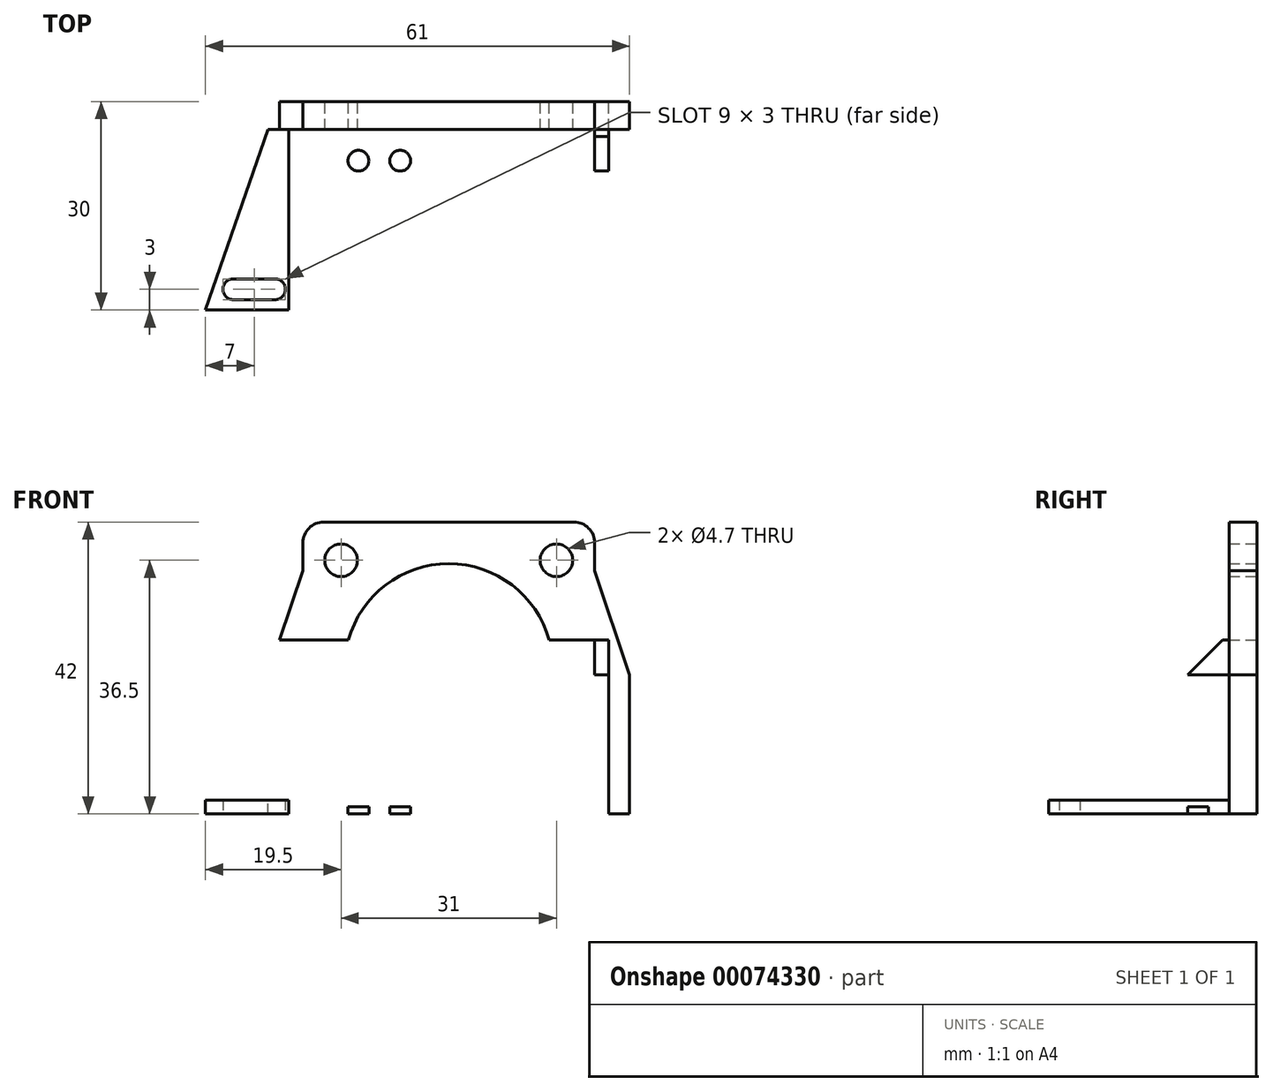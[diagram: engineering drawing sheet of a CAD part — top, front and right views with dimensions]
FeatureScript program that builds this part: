
annotation { "Feature Type Name" : "Feature", "Feature Type Description" : "" }
export const myFeature = defineFeature(function(context is Context, id is Id, definition is map)
    precondition{}
    {
        {
            var Q0;
            Q0=qCreatedBy(makeId("Front.planeOp"),FACE);
            var sketch = newSketch(context, id + "F0", { "sketchPlane" : qUnion([Q0])});
            skLineSegment(sketch, "E0.rect.bottom", {"start": v(21, 21) * mm, "end": v(-21, 21) * mm});
            skLineSegment(sketch, "E0.rect.top", {"start": v(21, -21) * mm, "end": v(-21, -21) * mm});
            skLineSegment(sketch, "E0.rect.left", {"start": v(21, 21) * mm, "end": v(21, -21) * mm});
            skLineSegment(sketch, "E0.rect.right", {"start": v(-21, 21) * mm, "end": v(-21, -21) * mm});
            skPoint(sketch, "E0.rect.middle", {"position": v(0, 0) * mm});
            skCircle(sketch, "E1", {"center": v(0, 0) * mm, "radius": 15 * mm});
            skCircle(sketch, "E2", {"center": v(-15.5, 15.5) * mm, "radius": 2.35 * mm});
            skCircle(sketch, "E3.MirrorC", {"center": v(15.5, 15.5) * mm, "radius": 2.35 * mm});
            skCircle(sketch, "E4.MirrorC", {"center": v(15.5, -15.5) * mm, "radius": 2.35 * mm});
            skCircle(sketch, "E5.MirrorC", {"center": v(-15.5, -15.5) * mm, "radius": 2.35 * mm});
            skLineSegment(sketch, "E6.bottom", {"start": v(21, -21) * mm, "end": v(26, -21) * mm});
            skLineSegment(sketch, "E6.top", {"start": v(21, -1) * mm, "end": v(26, -1) * mm});
            skLineSegment(sketch, "E6.left", {"start": v(21, -21) * mm, "end": v(21, -1) * mm});
            skLineSegment(sketch, "E6.right", {"start": v(26, -21) * mm, "end": v(26, -1) * mm});
            skLineSegment(sketch, "E7.MirrorCS", {"start": v(-21, -1) * mm, "end": v(-26, -1) * mm});
            skLineSegment(sketch, "E8.MirrorCS", {"start": v(-26, -21) * mm, "end": v(-26, -1) * mm});
            skLineSegment(sketch, "E9", {"start": v(26, -1) * mm, "end": v(21, 14) * mm});
            skLineSegment(sketch, "E10.MirrorCS", {"start": v(-26, -1) * mm, "end": v(-21, 14) * mm});
            skLineSegment(sketch, "E11.MirrorCS", {"start": v(-21, -21) * mm, "end": v(-26, -21) * mm});
            skLineSegment(sketch, "E12", {"start": v(-21, -20) * mm, "end": v(21, -20) * mm});
            skLineSegment(sketch, "E13.bottom", {"start": v(21, -21) * mm, "end": v(23, -21) * mm});
            skLineSegment(sketch, "E13.top", {"start": v(21, 4) * mm, "end": v(23, 4) * mm});
            skLineSegment(sketch, "E13.left", {"start": v(21, -21) * mm, "end": v(21, 4) * mm});
            skLineSegment(sketch, "E13.right", {"start": v(23, -21) * mm, "end": v(23, 4) * mm});
            skLineSegment(sketch, "E14.MirrorCS", {"start": v(-21, 4) * mm, "end": v(-23, 4) * mm});
            skLineSegment(sketch, "E15.MirrorCS", {"start": v(-23, -21) * mm, "end": v(-23, 4) * mm});
            skSolve(sketch);
        }
        {
            var Q0;
            {var subQ3=sQuery(id+"F0.wireOp",EDGE,"E0.rect.bottom");Q0=makeQuery(id+"F0.imprint","IMPRINT",FACE,{"disambiguationData":[TD([[makeQuery(id+"F0.imprint","IMPRINT",EDGE,{"derivedFrom":subQ3}),1.0]])]});}
            var Q1;
            {var subQ1=sQuery(id+"F0.wireOp",EDGE,"E9");Q1=makeQuery(id+"F0.imprint","IMPRINT",FACE,{"disambiguationData":[TD([[makeQuery(id+"F0.imprint","IMPRINT",EDGE,{"derivedFrom":subQ1}),1.0]])]});}
            var Q2;
            {var subQ1=sQuery(id+"F0.wireOp",EDGE,"E10.MirrorCS");Q2=makeQuery(id+"F0.imprint","IMPRINT",FACE,{"disambiguationData":[TD([[makeQuery(id+"F0.imprint","IMPRINT",EDGE,{"derivedFrom":subQ1}),-1.0]])]});}
            var Q3;
            {var subQ0=sQuery(id+"F0.wireOp",EDGE,"E6.bottom");Q3=makeQuery(id+"F0.imprint","IMPRINT",FACE,{"disambiguationData":[TD([[makeQuery(id+"F0.imprint","IMPRINT",EDGE,{"derivedFrom":subQ0}),1.0]])]});}
            var Q4;
            {var subQ0=sQuery(id+"F0.wireOp",EDGE,"E8.MirrorCS");Q4=makeQuery(id+"F0.imprint","IMPRINT",FACE,{"disambiguationData":[TD([[makeQuery(id+"F0.imprint","IMPRINT",EDGE,{"derivedFrom":subQ0}),-1.0]])]});}
            var Q5;
            {var subQ0=sQuery(id+"F0.wireOp",EDGE,"E0.rect.top");Q5=makeQuery(id+"F0.imprint","IMPRINT",FACE,{"disambiguationData":[TD([[makeQuery(id+"F0.imprint","IMPRINT",EDGE,{"derivedFrom":subQ0}),-1.0]])]});}
            extrude(context, id + "F1", {"entities" : qUnion([Q0, Q1, Q2, Q3, Q4, Q5]), "depth" : 4 * mm});
        }
        {
            var Q0;
            {var subQ5=sQuery(id+"F0.wireOp",EDGE,"E13.top");Q0=makeQuery(id+"F0.imprint","IMPRINT",FACE,{"disambiguationData":[TD([[makeQuery(id+"F0.imprint","IMPRINT",EDGE,{"derivedFrom":subQ5}),-1.0]])]});}
            var Q1;
            {var subQ0=sQuery(id+"F0.wireOp",EDGE,"E13.bottom");Q1=makeQuery(id+"F0.imprint","IMPRINT",FACE,{"disambiguationData":[TD([[makeQuery(id+"F0.imprint","IMPRINT",EDGE,{"derivedFrom":subQ0}),1.0]])]});}
            var Q2;
            {var subQ3=sQuery(id+"F0.wireOp",EDGE,"E14.MirrorCS");Q2=makeQuery(id+"F0.imprint","IMPRINT",FACE,{"disambiguationData":[TD([[makeQuery(id+"F0.imprint","IMPRINT",EDGE,{"derivedFrom":subQ3}),1.0]])]});}
            var Q3;
            {var subQ1=sQuery(id+"F0.wireOp",EDGE,"E0.rect.right");var subQ5=sQuery(id+"F0.wireOp",EDGE,"E7.MirrorCS");var subQ6=makeQuery(id+"F0.imprint","INTERSECT",VERTEX,{"derivedFrom":[subQ1,subQ5]});Q3=makeQuery(id+"F0.imprint","IMPRINT",FACE,{"disambiguationData":[TD([[makeQuery(id+"F0.imprint","IMPRINT",EDGE,{"disambiguationData":[TD([[subQ6,-1.0]])],"derivedFrom":subQ1}),-1.0]])]});}
            var Q4;
            {var subQ0=sQuery(id+"F0.wireOp",EDGE,"E0.rect.top");Q4=makeQuery(id+"F0.imprint","IMPRINT",FACE,{"disambiguationData":[TD([[makeQuery(id+"F0.imprint","IMPRINT",EDGE,{"derivedFrom":subQ0}),-1.0]])]});}
            extrude(context, id + "F2", {"entities" : qUnion([Q0, Q1, Q2, Q3, Q4]), "operationType" : NewBodyOperationType.ADD, "depth" : 30 * mm});
        }
        {
            var Q0;
            Q0=makeQuery(id+"F2.opExtrude","SWEPT_FACE",FACE,{"disambiguationData":[OSD([sQuery(id+"F0.wireOp",EDGE,"E13.right")])]});
            var sketch = newSketch(context, id + "F3", { "sketchPlane" : qUnion([Q0])});
            skLineSegment(sketch, "E16", {"start": v(-5, 4) * mm, "end": v(-30, -21) * mm});
            skSolve(sketch);
        }
        {
            var Q0;
            {var subQ0=sQuery(id+"F3.wireOp",EDGE,"E16");Q0=makeQuery(id+"F3.imprint","IMPRINT",FACE,{"disambiguationData":[TD([[makeQuery(id+"F3.imprint","IMPRINT",EDGE,{"derivedFrom":subQ0}),-1.0]])]});}
            extrude(context, id + "F4", {"entities" : qUnion([Q0]), "operationType" : NewBodyOperationType.REMOVE, "endBound" : BoundingType.THROUGH_ALL, "oppositeDirection" : true, "depth" : 25 * mm});
        }
        {
            var Q0;
            {var subQ0=sQuery(id+"F0.wireOp",EDGE,"E11.MirrorCS");var subQ1=sQuery(id+"F0.wireOp",EDGE,"E0.rect.top");Q0=makeQuery(id+"F2.boolean.opBoolean","MERGE",FACE,{"derivedFrom":[makeQuery(id+"F1.opExtrude","SWEPT_FACE",FACE,{"disambiguationData":[OSD([subQ1])]}),makeQuery(id+"F1.opExtrude","SWEPT_FACE",FACE,{"disambiguationData":[OSD([sQuery(id+"F0.wireOp",EDGE,"E6.bottom")])]}),makeQuery(id+"F1.opExtrude","SWEPT_FACE",FACE,{"disambiguationData":[OSD([subQ0])]}),makeQuery(id+"F2.opExtrude","SWEPT_FACE",FACE,{"disambiguationData":[OSD([subQ1,subQ0,sQuery(id+"F0.wireOp",EDGE,"E13.bottom")])]})]});}
            var sketch = newSketch(context, id + "F5", { "sketchPlane" : qUnion([Q0])});
            skLineSegment(sketch, "E17", {"start": v(26, 4) * mm, "end": v(35, 30) * mm});
            skLineSegment(sketch, "E18", {"start": v(35, 30) * mm, "end": v(23, 30) * mm});
            skLineSegment(sketch, "E19.MirrorCS", {"start": v(-35, 30) * mm, "end": v(-23, 30) * mm});
            skLineSegment(sketch, "E20.MirrorCS", {"start": v(-26, 4) * mm, "end": v(-35, 30) * mm});
            skCircle(sketch, "E21", {"center": v(25, 27) * mm, "radius": 1.5 * mm});
            skCircle(sketch, "E22", {"center": v(31, 27) * mm, "radius": 1.5 * mm});
            skLineSegment(sketch, "E23", {"start": v(25, 25.5) * mm, "end": v(31, 25.5) * mm});
            skLineSegment(sketch, "E24", {"start": v(25, 28.5) * mm, "end": v(31, 28.5) * mm});
            skCircle(sketch, "E25.MirrorC", {"center": v(-25, 27) * mm, "radius": 1.5 * mm});
            skCircle(sketch, "E26.MirrorC", {"center": v(-31, 27) * mm, "radius": 1.5 * mm});
            skLineSegment(sketch, "E27.MirrorCS", {"start": v(-25, 28.5) * mm, "end": v(-31, 28.5) * mm});
            skLineSegment(sketch, "E28.MirrorCS", {"start": v(-25, 25.5) * mm, "end": v(-31, 25.5) * mm});
            skLineSegment(sketch, "E29", {"start": v(7, 10) * mm, "end": v(13, 10) * mm});
            skLineSegment(sketch, "E30", {"start": v(7, 7) * mm, "end": v(13, 7) * mm});
            skCircle(sketch, "E31", {"center": v(13, 8.5) * mm, "radius": 1.5 * mm});
            skCircle(sketch, "E32", {"center": v(7, 8.5) * mm, "radius": 1.5 * mm});
            skCircle(sketch, "E33.MirrorC", {"center": v(-7, 8.5) * mm, "radius": 1.5 * mm});
            skLineSegment(sketch, "E34.MirrorCS", {"start": v(-7, 10) * mm, "end": v(-13, 10) * mm});
            skCircle(sketch, "E35.MirrorC", {"center": v(-13, 8.5) * mm, "radius": 1.5 * mm});
            skLineSegment(sketch, "E36.MirrorCS", {"start": v(-7, 7) * mm, "end": v(-13, 7) * mm});
            skSolve(sketch);
        }
        {
            var Q0;
            Q0=makeQuery(id+"F5.imprint","IMPRINT",FACE,{"disambiguationData":[TD([[makeQuery(id+"F5.imprint","IMPRINT",EDGE,{"derivedFrom":sQuery(id+"F5.wireOp",EDGE,"E19.MirrorCS")}),-1.0]])]});
            var Q1;
            Q1=makeQuery(id+"F5.imprint","IMPRINT",FACE,{"disambiguationData":[TD([[makeQuery(id+"F5.imprint","IMPRINT",EDGE,{"derivedFrom":sQuery(id+"F5.wireOp",EDGE,"E17")}),1.0]])]});
            extrude(context, id + "F6", {"entities" : qUnion([Q0, Q1]), "operationType" : NewBodyOperationType.ADD, "oppositeDirection" : true, "depth" : 2 * mm});
        }
        {
            var Q0;
            {var subQ0=sQuery(id+"F5.wireOp",EDGE,"E34.MirrorCS");Q0=makeQuery(id+"F5.imprint","IMPRINT",FACE,{"disambiguationData":[TD([[makeQuery(id+"F5.imprint","IMPRINT",EDGE,{"derivedFrom":subQ0}),1.0]])]});}
            var Q1;
            {var subQ0=sQuery(id+"F5.wireOp",EDGE,"E35.MirrorC");var subQ1=makeQuery(id+"F5.imprint","INTERSECT",VERTEX,{"derivedFrom":[sQuery(id+"F5.wireOp",EDGE,"E34.MirrorCS"),subQ0]});Q1=makeQuery(id+"F5.imprint","IMPRINT",FACE,{"disambiguationData":[TD([[makeQuery(id+"F5.imprint","IMPRINT",EDGE,{"disambiguationData":[TD([[subQ1,-1.0]])],"derivedFrom":subQ0}),-1.0]])]});}
            var Q2;
            {var subQ0=sQuery(id+"F5.wireOp",EDGE,"E33.MirrorC");var subQ1=makeQuery(id+"F5.imprint","INTERSECT",VERTEX,{"derivedFrom":[subQ0,sQuery(id+"F5.wireOp",EDGE,"E34.MirrorCS")]});Q2=makeQuery(id+"F5.imprint","IMPRINT",FACE,{"disambiguationData":[TD([[makeQuery(id+"F5.imprint","IMPRINT",EDGE,{"disambiguationData":[TD([[subQ1,-1.0]])],"derivedFrom":subQ0}),-1.0]])]});}
            var Q3;
            {var subQ0=sQuery(id+"F5.wireOp",EDGE,"E29");Q3=makeQuery(id+"F5.imprint","IMPRINT",FACE,{"disambiguationData":[TD([[makeQuery(id+"F5.imprint","IMPRINT",EDGE,{"derivedFrom":subQ0}),-1.0]])]});}
            var Q4;
            {var subQ0=sQuery(id+"F5.wireOp",EDGE,"E31");var subQ1=makeQuery(id+"F5.imprint","INTERSECT",VERTEX,{"derivedFrom":[sQuery(id+"F5.wireOp",EDGE,"E29"),subQ0]});Q4=makeQuery(id+"F5.imprint","IMPRINT",FACE,{"disambiguationData":[TD([[makeQuery(id+"F5.imprint","IMPRINT",EDGE,{"disambiguationData":[TD([[subQ1,-1.0]])],"derivedFrom":subQ0}),1.0]])]});}
            var Q5;
            {var subQ0=sQuery(id+"F5.wireOp",EDGE,"E32");var subQ1=makeQuery(id+"F5.imprint","INTERSECT",VERTEX,{"derivedFrom":[sQuery(id+"F5.wireOp",EDGE,"E29"),subQ0]});Q5=makeQuery(id+"F5.imprint","IMPRINT",FACE,{"disambiguationData":[TD([[makeQuery(id+"F5.imprint","IMPRINT",EDGE,{"disambiguationData":[TD([[subQ1,-1.0]])],"derivedFrom":subQ0}),1.0]])]});}
            extrude(context, id + "F7", {"entities" : qUnion([Q0, Q1, Q2, Q3, Q4, Q5]), "operationType" : NewBodyOperationType.REMOVE, "oppositeDirection" : true, "depth" : 25 * mm});
        }
        {
            var Q0;
            Q0=makeQuery(id+"F1.opExtrude","SWEPT_EDGE",EDGE,{"disambiguationData":[OSD([sQuery(id+"F0.wireOp",EDGE,"E0.rect.bottom"),sQuery(id+"F0.wireOp",EDGE,"E0.rect.left")])]});
            var Q1;
            Q1=makeQuery(id+"F1.opExtrude","SWEPT_EDGE",EDGE,{"disambiguationData":[OSD([sQuery(id+"F0.wireOp",EDGE,"E0.rect.bottom"),sQuery(id+"F0.wireOp",EDGE,"E0.rect.right")])]});
            fillet(context, id + "F8", {"entities" : qUnion([Q0, Q1]), "radius" : 3 * mm, "tangentPropagation" : true, "allowEdgeOverflow" : false});
        }
    });
